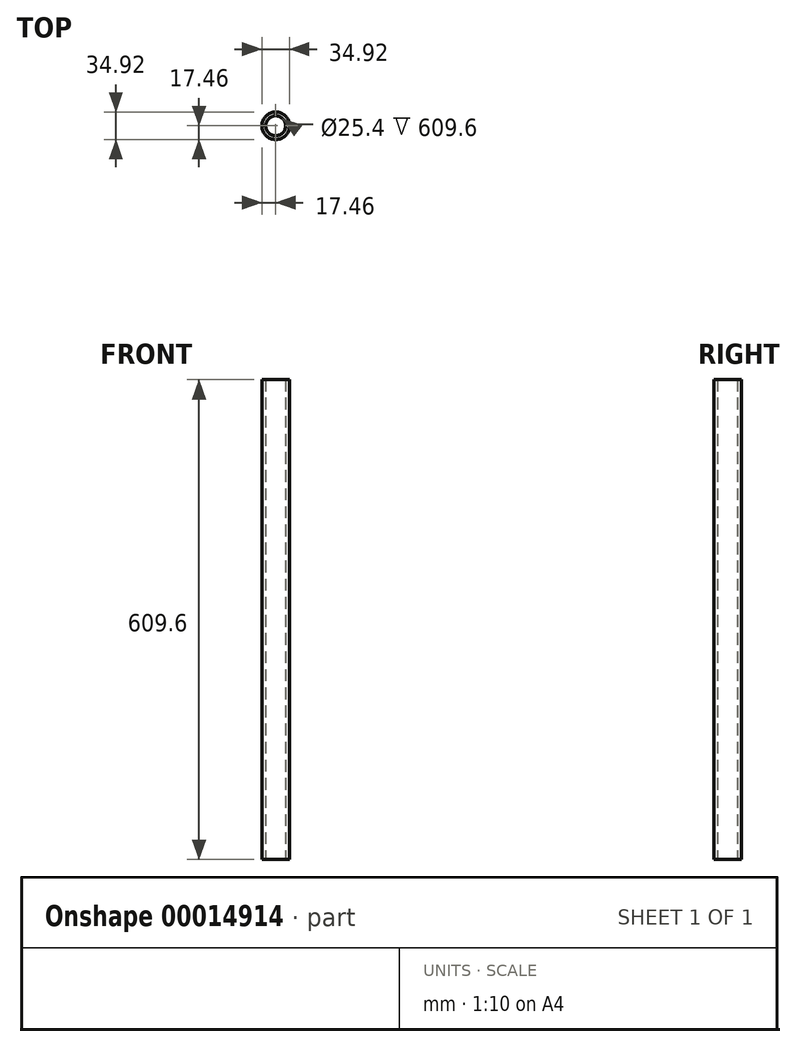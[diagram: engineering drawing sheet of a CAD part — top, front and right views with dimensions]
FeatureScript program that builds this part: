
annotation { "Feature Type Name" : "Feature", "Feature Type Description" : "" }
export const myFeature = defineFeature(function(context is Context, id is Id, definition is map)
    precondition{}
    {
        {
            var Q0;
            Q0=qCreatedBy(makeId("Top.planeOp"),FACE);
            var sketch = newSketch(context, id + "F0", { "sketchPlane" : qUnion([Q0])});
            skCircle(sketch, "E0", {"center": v(0, 0) * mm, "radius": 12.7 * mm});
            skCircle(sketch, "E1", {"center": v(0, 0) * mm, "radius": 17.46 * mm});
            skSolve(sketch);
        }
        {
            var Q0;
            Q0=makeQuery(id+"F0.imprint","IMPRINT",FACE,{"disambiguationData":[TD([[makeQuery(id+"F0.imprint","IMPRINT",EDGE,{"derivedFrom":sQuery(id+"F0.wireOp",EDGE,"E0")}),-1.0]])]});
            extrude(context, id + "F1", {"entities" : qUnion([Q0]), "depth" : 609.6 * mm});
        }
    });
